# Revit family: Legrand universal flush floor boxes NL
name_source: partatom
category: Installations électriques
units: mm (PartAtom-declared; Revit-internal decimal feet)

## family parameters
Conserver l'orientation des annotations = Non
Cote de connecteur circulaire = Utiliser le diamètre
Couper avec des vides une fois chargée = Non
Hôte = Face
Partagée = Non
Point de calcul de pièce = Non
Type d'élément = Normal

## types (9) — shared parameters
00 = Reservation boitier : 00
000000 = Accessoire : Aucun
01 = Reservation boitier : 01
02 = Reservation boitier : 02
088026 = Accessoire : 088026
088027 = Accessoire : 088027
088028 = Accessoire : 088028
088080 = Boitier d'encastrement : 088080
088081 = Accessoire : 088081
088082 = Accessoire : 088082
088083 = Accessoire : 088083
088086 = Accessoire : 088086 + 088088+088142
088086-2 = Accessoire : 088086 + (2x088088)+088142
088090 = Boitier d'encastrement : 088090
088091 = Boitier d'encastrement : 088091
088092 = Boitier d'encastrement : 088092
088103 = Couvercle : 088103
088104 = Couvercle : 088104
088105 = Couvercle : 088105
088106 = Couvercle : 088106
088107 = Couvercle : 088107
088108 = Couvercle : 088108
088145 = Plaque finition : 088145
088146 = Plaque finition : 088146
088147 = Plaque finition : 088147
088148 = Plaque finition : 088148
088149 = Plaque finition : 088149
088150 = Plaque finition : 088150
26 = Reservation boitier : 26
27 = Reservation boitier : 27
28 = Reservation boitier : 28
80 = Reservation boitier : 80
90 = Reservation boitier : 90
91 = Reservation boitier : 91
92 = Reservation boitier : 92
Auto = Type of floor : Auto adjustable
Brass = Finish : Brass
Fabricant = LEGRAND
Inox = Finish : Stainless steel
StdB125 = Type of floor : In-screed under 125 mm
StdB170 = Type of floor : In-screed above 125 mm and under 170 mm
StdB250 = Type of floor : In-screed above 170 mm and under 250 mm
StdT = Type of floor : Raised floor
zero-valued in all types: Elévation par défaut

## per-type parameters (varying)
| type | Description | Frames | Support | Support appareillage |
| 8 modules 2x4 | Universal flush floor box 8 modules vertical | 088123 | 23 | Support appareillage : 088123 |
| 12 modules 2x6 | Universal flush floor box 12 modules vertical | 088124 | 24 | Support appareillage : 088124 |
| 16 modules 2x8 | Universal flush floor box 16 modules vertical | 088125 | 25 | Support appareillage : 088125 |
| 12 modules 3x4 | Universal flush floor box 12 modules horizontal adjustable | 088120 | 20 | Support appareillage : 088120 |
| 18 modules 3x6 | Universal flush floor box 18 modules horizontal adjustable | 088121 | 21 | Support appareillage : 088121 |
| 24 modules 3x8 | Universal flush floor box 24 modules horizontal adjustable | 088122 | 22 | Support appareillage : 088122 |
| Open frame 8-12 modules | Flush access unit 8/12 modules | 088139 | 39 | Support appareillage : 088139 |
| Open frame 12-18 modules | Flush access unit 12/18 modules | 088140 | 40 | Support appareillage : 088140 |
| Open frame 16-24 modules | Flush access unit 16/24 modules | 088141 | 41 | Support appareillage : 088141 |
